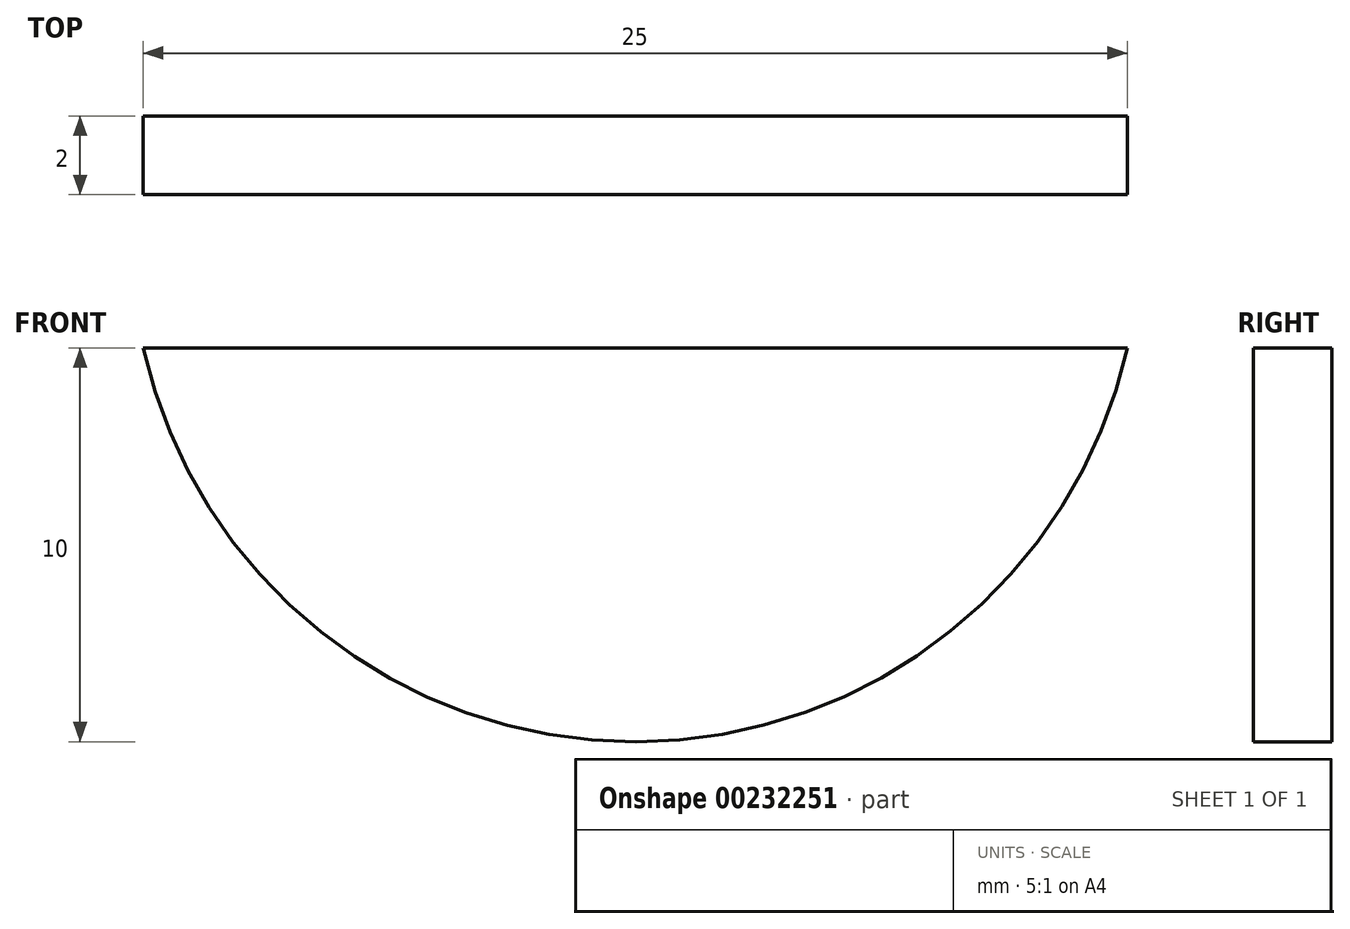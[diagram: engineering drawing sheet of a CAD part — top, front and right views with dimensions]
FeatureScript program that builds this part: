
annotation { "Feature Type Name" : "Feature", "Feature Type Description" : "" }
export const myFeature = defineFeature(function(context is Context, id is Id, definition is map)
    precondition{}
    {
        {
            var Q0;
            Q0=qCreatedBy(makeId("Front.planeOp"),FACE);
            var sketch = newSketch(context, id + "F0", { "sketchPlane" : qUnion([Q0])});
            skLineSegment(sketch, "E0.bottom", {"start": v(-23.75, 11.7) * mm, "end": v(1.25, 11.7) * mm});
            skLineSegment(sketch, "E0.left", {"start": v(-23.75, 11.7) * mm, "end": v(-23.74, 11.67) * mm});
            skLineSegment(sketch, "E0.right", {"start": v(1.25, 11.7) * mm, "end": v(1.25, 11.7) * mm});
            skArc(sketch, "E1", {"start": v(-23.75, 11.7) * mm, "mid": v(-11.25, 1.7) * mm, "end": v(1.25, 11.7) * mm});
            skSolve(sketch);
        }
        {
            var Q0;
            Q0=makeQuery(id+"F0.imprint","IMPRINT",FACE,{"disambiguationData":[TD([[makeQuery(id+"F0.imprint","IMPRINT",EDGE,{"derivedFrom":sQuery(id+"F0.wireOp",EDGE,"E0.bottom")}),-1.0]])]});
            extrude(context, id + "F1", {"entities" : qUnion([Q0]), "depth" : 2 * mm});
        }
    });
